# Revit family: Pump_Commercial-Effluent-Zoeller-152-153
name_source: partatom
category: Mechanical Equipment
revit_build: Autodesk Revit 2014 (Build: 20130308_1515(x64)
units: mm (PartAtom-declared; Revit-internal decimal feet)

## types (4) — shared parameters
Assembly Code = D2010900
Cord Length = 240"
Cord Type = UL listed
Default Elevation = 0"
Description = Commercial Sewage Pumps
Discharge Diameter = 1 1/2" NPT
Discharge Height = 5 3/8"
Discharge Radius = 3/4"
Height = 12 1/8"
Hertz = 60
Impeller Type = Non-clogging thermoplastic vortex design
Installation Type = Floor Mounted
Insulation = Class B
Lead Wires Insulation = Class B
Length = 10 3/32"
Manufacturer = Zoeller
Material = Cast Iron-Zoeller-Powder Coated Epoxy
Max. Water Temp. = 130 °F
Minimum Head = 60"
Model = 153
Motor Design Letter = NEMA B
Motor Thermal Shutoff = Auto Reset Thermal Overload.
Motor Type = Submersible
O-Rings and Cover Gasket = Neoprene
Operation = Permanent Split Capacitor
Phase = 1
Price = Prices may vary. Please consult Manufacturer Representative for most up-to-date price list.
Product Page URL = http://www.zoellerpumps.com
Service Factor = 1.15
Shaft Seal = Carbon/Ceramic
Type = Permanent Split Capacitor
URL = http://www.zoellerpumps.com
Warranty Information = 36 Months (Limited)
Waste Connection = Yes
Width = 7 3/4"

## per-type parameters (varying)
| type | Amps | Apparent Load | Max Flow @ 5' | Maximum Head | Motor | Voltage |
| 153 - 115V 1Ph | 11 A | 1208 VA | 77 GPM | 528" | 1/2 HP | 115 V |
| 152 - 115V 1Ph | 9 A | 978 VA | 69 GPM | 456" | .4 HP | 115 V |
| 152 - 230V 1Ph | 4 A | 989 VA | 69 GPM | 456" | .4 HP | 230 V |
| 153 - 230V 1Ph | 5 A | 1219 VA | 77 GPM | 528" | 1/2 HP | 230 V |

## geometry (parser evidence)
native form markers: Sweep x1
no freeform markers — native parametric forms only
